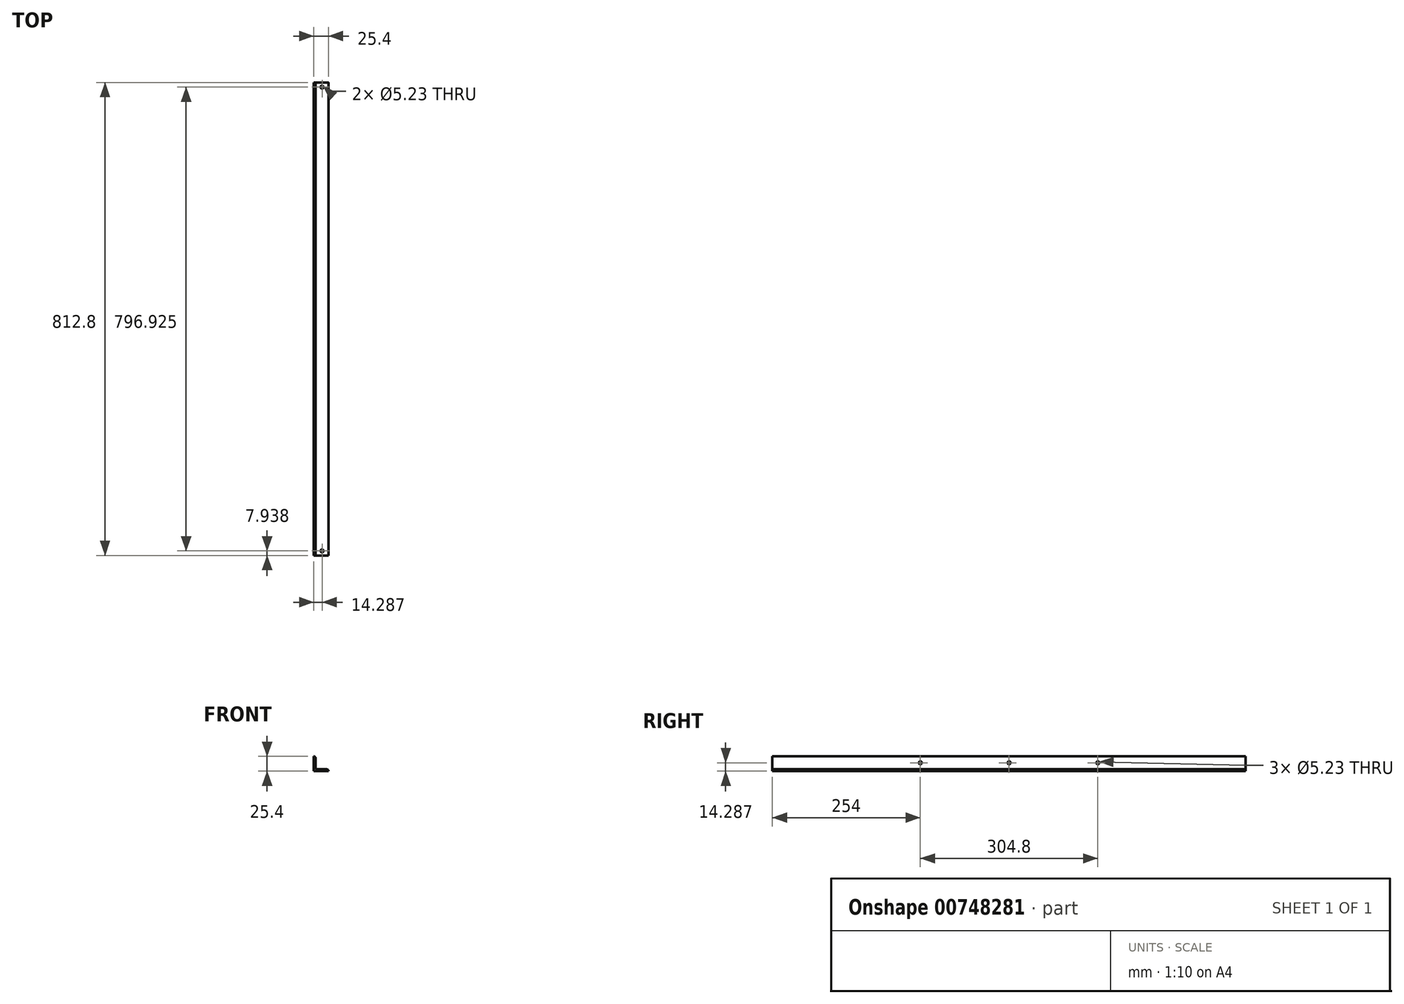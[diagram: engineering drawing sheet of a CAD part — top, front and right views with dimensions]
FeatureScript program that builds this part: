
annotation { "Feature Type Name" : "Feature", "Feature Type Description" : "" }
export const myFeature = defineFeature(function(context is Context, id is Id, definition is map)
    precondition{}
    {
        {
            var Q0;
            Q0=qCreatedBy(makeId("Front.planeOp"),FACE);
            var sketch = newSketch(context, id + "F0", { "sketchPlane" : qUnion([Q0])});
            skLineSegment(sketch, "E0", {"start": v(0, 0) * mm, "end": v(-25.4, 0) * mm});
            skLineSegment(sketch, "E1", {"start": v(-25.4, 0) * mm, "end": v(-25.4, 25.4) * mm});
            skLineSegment(sketch, "E2", {"start": v(-25.4, 25.4) * mm, "end": v(-25.4, 25.4) * mm});
            skLineSegment(sketch, "E3", {"start": v(-22.23, 22.23) * mm, "end": v(-22.23, 6.35) * mm});
            skLineSegment(sketch, "E4", {"start": v(-19.05, 3.18) * mm, "end": v(-3.18, 3.18) * mm});
            skLineSegment(sketch, "E5", {"start": v(0, 0) * mm, "end": v(0, 0) * mm});
            skPoint(sketch, "E6.visualSharp", {"position": v(-22.23, 3.18) * mm});
            skArc(sketch, "E6.filletArc", {"start": v(-22.23, 6.35) * mm, "mid": v(-21.3, 4.1) * mm, "end": v(-19.05, 3.18) * mm});
            skPoint(sketch, "E7.visualSharp", {"position": v(-22.23, 25.4) * mm});
            skArc(sketch, "E7.filletArc", {"start": v(-22.23, 22.23) * mm, "mid": v(-23.15, 24.47) * mm, "end": v(-25.4, 25.4) * mm});
            skPoint(sketch, "E8.visualSharp", {"position": v(0, 3.18) * mm});
            skArc(sketch, "E8.filletArc", {"start": v(0, 0) * mm, "mid": v(-0.93, 2.25) * mm, "end": v(-3.18, 3.18) * mm});
            skSolve(sketch);
        }
        {
            var Q0;
            Q0 = qSketchRegion(id + "F0", true);
            extrude(context, id + "F1", {"entities" : qUnion([Q0]), "depth" : 812.8 * mm, "offsetDistance" : 25.4 * mm});
        }
        {
            var Q0;
            Q0=makeQuery(id+"F1.opExtrude","SWEPT_FACE",FACE,{"disambiguationData":[OSD([sQuery(id+"F0.wireOp",EDGE,"E3")])]});
            var sketch = newSketch(context, id + "F2", { "sketchPlane" : qUnion([Q0])});
            skLineSegment(sketch, "E9", {"start": v(-406.4, 6.35) * mm, "end": v(-406.4, 22.23) * mm, "construction": true});
            skLineSegment(sketch, "E10.0", {"start": v(-558.8, 6.35) * mm, "end": v(-558.8, 22.22) * mm, "construction": true});
            skLineSegment(sketch, "E11.0", {"start": v(-254, 6.35) * mm, "end": v(-254, 22.23) * mm, "construction": true});
            skLineSegment(sketch, "E12", {"start": v(-812.8, 14.29) * mm, "end": v(0, 14.29) * mm, "construction": true});
            skCircle(sketch, "E13", {"center": v(-558.8, 14.29) * mm, "radius": 2.62 * mm});
            skCircle(sketch, "E14", {"center": v(-406.4, 14.29) * mm, "radius": 2.62 * mm});
            skCircle(sketch, "E15", {"center": v(-254, 14.29) * mm, "radius": 2.62 * mm});
            skSolve(sketch);
        }
        {
            var Q0;
            Q0 = qSketchRegion(id + "F2", true);
            extrude(context, id + "F3", {"entities" : qUnion([Q0]), "operationType" : NewBodyOperationType.REMOVE, "endBound" : BoundingType.THROUGH_ALL, "oppositeDirection" : true, "depth" : 25.4 * mm, "offsetDistance" : 25.4 * mm});
        }
        {
            var Q0;
            Q0=makeQuery(id+"F1.opExtrude","SWEPT_FACE",FACE,{"disambiguationData":[OSD([sQuery(id+"F0.wireOp",EDGE,"E4")])]});
            var sketch = newSketch(context, id + "F4", { "sketchPlane" : qUnion([Q0])});
            skLineSegment(sketch, "E16", {"start": v(-11.11, -812.8) * mm, "end": v(-11.11, 0) * mm, "construction": true});
            skLineSegment(sketch, "E17", {"start": v(-3.18, -804.86) * mm, "end": v(-19.05, -804.86) * mm, "construction": true});
            skCircle(sketch, "E18", {"center": v(-11.11, -804.86) * mm, "radius": 2.62 * mm});
            skLineSegment(sketch, "E19", {"start": v(-19.05, -7.94) * mm, "end": v(-3.18, -7.94) * mm, "construction": true});
            skCircle(sketch, "E20", {"center": v(-11.11, -7.94) * mm, "radius": 2.62 * mm});
            skSolve(sketch);
        }
        {
            var Q0;
            Q0 = qSketchRegion(id + "F4", true);
            extrude(context, id + "F5", {"entities" : qUnion([Q0]), "operationType" : NewBodyOperationType.REMOVE, "endBound" : BoundingType.THROUGH_ALL, "oppositeDirection" : true, "depth" : 25.4 * mm, "offsetDistance" : 25.4 * mm});
        }
    });
